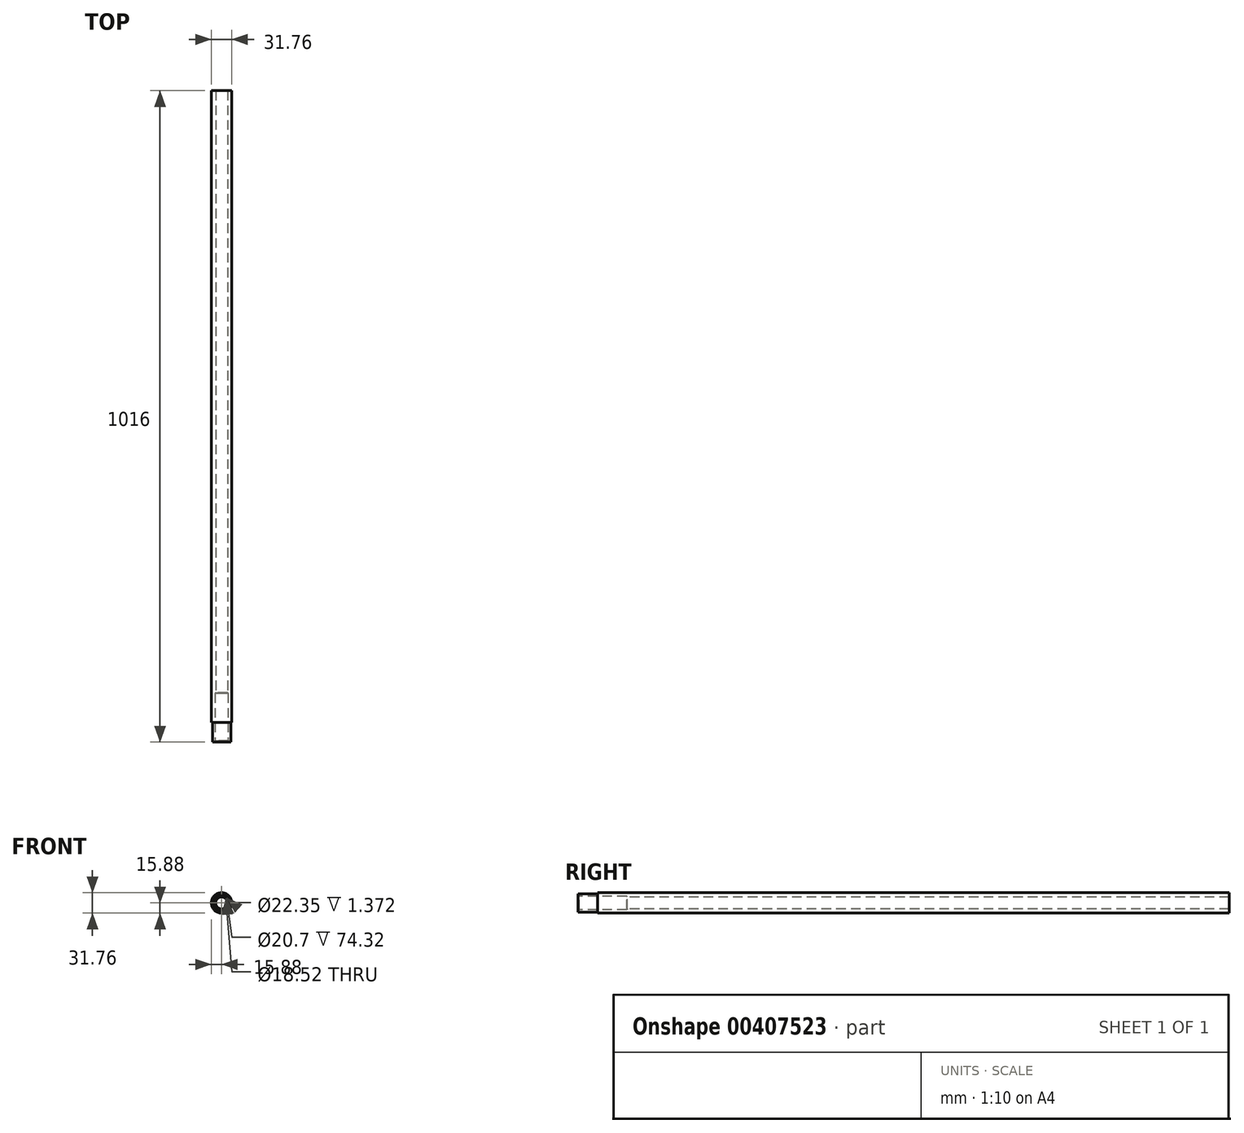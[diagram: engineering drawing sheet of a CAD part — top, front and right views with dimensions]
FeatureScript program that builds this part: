
annotation { "Feature Type Name" : "Feature", "Feature Type Description" : "" }
export const myFeature = defineFeature(function(context is Context, id is Id, definition is map)
    precondition{}
    {
        {
            var Q0;
            Q0=qCreatedBy(makeId("Front.planeOp"),FACE);
            var sketch = newSketch(context, id + "F0", { "sketchPlane" : qUnion([Q0])});
            skCircle(sketch, "E0", {"center": v(0, 0) * mm, "radius": 15.88 * mm});
            skSolve(sketch);
        }
        {
            var Q0;
            Q0=makeQuery(id+"F0.imprint","IMPRINT",FACE,{"disambiguationData":[TD([[makeQuery(id+"F0.imprint","IMPRINT",EDGE,{"derivedFrom":sQuery(id+"F0.wireOp",EDGE,"E0")}),1.0]])]});
            extrude(context, id + "F1", {"entities" : qUnion([Q0]), "depth" : 1016 * mm});
        }
        {
            var Q0;
            Q0=makeQuery(id+"F1.opExtrude","CAP_FACE",FACE,{"disambiguationData":[OSD([sQuery(id+"F0.wireOp",EDGE,"E0")])],"isStart":false});
            var sketch = newSketch(context, id + "F2", { "sketchPlane" : qUnion([Q0])});
            skCircle(sketch, "E1", {"center": v(0, 0) * mm, "radius": 11.18 * mm});
            skSolve(sketch);
        }
        {
            var Q0;
            Q0=makeQuery(id+"F2.imprint","IMPRINT",FACE,{"disambiguationData":[TD([[makeQuery(id+"F2.imprint","IMPRINT",EDGE,{"derivedFrom":sQuery(id+"F2.wireOp",EDGE,"E1")}),1.0]])]});
            extrude(context, id + "F3", {"entities" : qUnion([Q0]), "operationType" : NewBodyOperationType.REMOVE, "oppositeDirection" : true, "depth" : 1.88 * mm});
        }
        {
            var Q0;
            Q0=makeQuery(id+"F1.opExtrude","CAP_FACE",FACE,{"disambiguationData":[OSD([sQuery(id+"F0.wireOp",EDGE,"E0")])],"isStart":false});
            var sketch = newSketch(context, id + "F4", { "sketchPlane" : qUnion([Q0])});
            skCircle(sketch, "E2", {"center": v(0, 0) * mm, "radius": 10.35 * mm});
            skSolve(sketch);
        }
        {
            var Q0;
            Q0 = qSketchRegion(id + "F4", true);
            extrude(context, id + "F5", {"entities" : qUnion([Q0]), "operationType" : NewBodyOperationType.REMOVE, "oppositeDirection" : true, "depth" : 76.2 * mm});
        }
        {
            var Q0;
            Q0=makeQuery(id+"F1.opExtrude","CAP_FACE",FACE,{"disambiguationData":[OSD([sQuery(id+"F0.wireOp",EDGE,"E0")])],"isStart":false});
            var sketch = newSketch(context, id + "F6", { "sketchPlane" : qUnion([Q0])});
            skCircle(sketch, "E3", {"center": v(0, 0) * mm, "radius": 9.26 * mm});
            skSolve(sketch);
        }
        {
            var Q0;
            Q0=makeQuery(id+"F6.imprint","IMPRINT",FACE,{"disambiguationData":[TD([[makeQuery(id+"F6.imprint","IMPRINT",EDGE,{"derivedFrom":sQuery(id+"F6.wireOp",EDGE,"E3")}),1.0]])]});
            extrude(context, id + "F7", {"entities" : qUnion([Q0]), "operationType" : NewBodyOperationType.REMOVE, "endBound" : BoundingType.THROUGH_ALL, "oppositeDirection" : true, "depth" : 25.4 * mm});
        }
        {
            var Q0;
            Q0=makeQuery(id+"F3.boolean.opBoolean","COPY",EDGE,{"derivedFrom":makeQuery(id+"F3.opExtrude","CAP_EDGE",EDGE,{"disambiguationData":[OSD([sQuery(id+"F2.wireOp",EDGE,"E1")])],"isStart":false})});
            fillet(context, id + "F8", {"entities" : qUnion([Q0]), "radius" : 0.5 * mm, "tangentPropagation" : true, "allowEdgeOverflow" : false});
        }
        {
            var Q0;
            Q0=makeQuery(id+"F1.opExtrude","CAP_FACE",FACE,{"disambiguationData":[OSD([sQuery(id+"F0.wireOp",EDGE,"E0")])],"isStart":false});
            var sketch = newSketch(context, id + "F9", { "sketchPlane" : qUnion([Q0])});
            skCircle(sketch, "E4", {"center": v(0, 0) * mm, "radius": 14.29 * mm});
            skCircle(sketch, "E5", {"center": v(0, 0) * mm, "radius": 15.88 * mm});
            skSolve(sketch);
        }
        {
            var Q0;
            Q0=makeQuery(id+"F9.imprint","IMPRINT",FACE,{"disambiguationData":[TD([[makeQuery(id+"F9.imprint","IMPRINT",EDGE,{"derivedFrom":sQuery(id+"F9.wireOp",EDGE,"E4")}),-1.0]])]});
            extrude(context, id + "F10", {"entities" : qUnion([Q0]), "operationType" : NewBodyOperationType.REMOVE, "oppositeDirection" : true, "depth" : 30.48 * mm});
        }
        {
            var Q0;
            Q0=makeQuery(id+"F7.boolean.opBoolean","INTERSECT",EDGE,{"derivedFrom":[makeQuery(id+"F5.boolean.opBoolean","COPY",FACE,{"derivedFrom":makeQuery(id+"F5.opExtrude","CAP_FACE",FACE,{"disambiguationData":[OSD([sQuery(id+"F4.wireOp",EDGE,"E2")])],"isStart":false})}),makeQuery(id+"F7.opExtrude","SWEPT_FACE",FACE,{"disambiguationData":[OSD([sQuery(id+"F6.wireOp",EDGE,"E3")])]})]});
            chamfer(context, id + "F11", {"entities" : qUnion([Q0]), "width" : 1.02 * mm, "tangentPropagation" : true});
        }
    });
